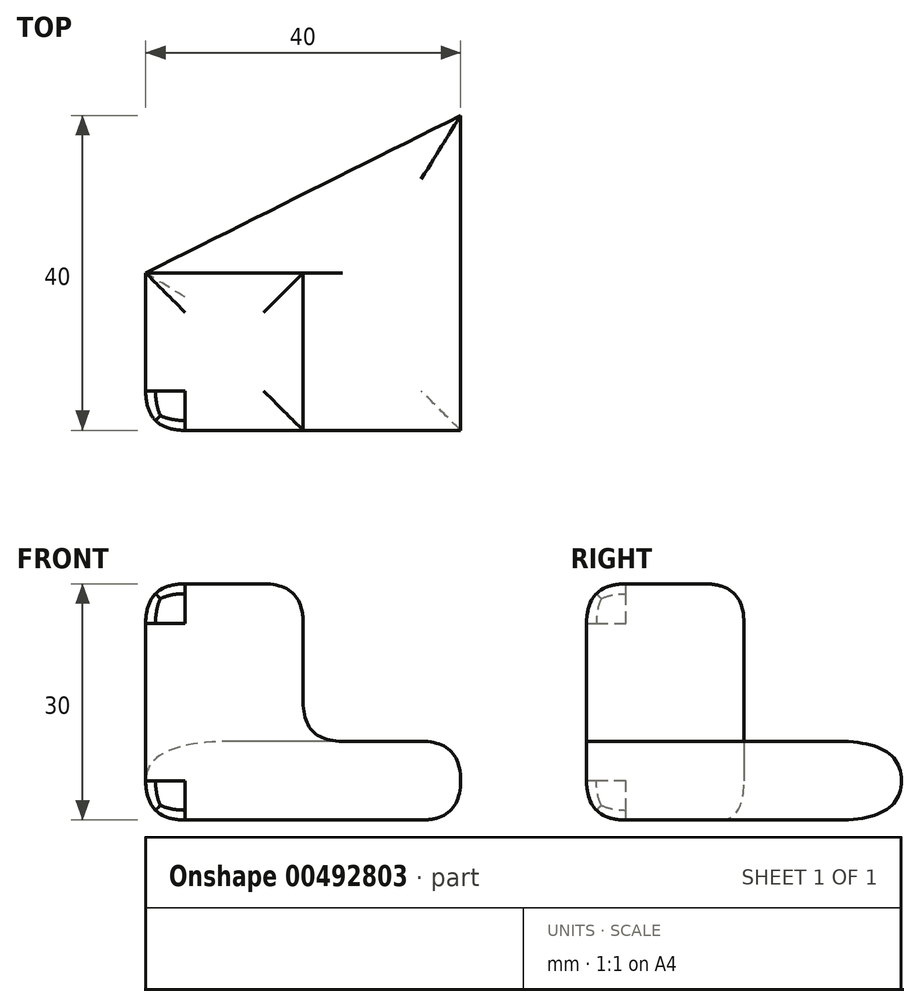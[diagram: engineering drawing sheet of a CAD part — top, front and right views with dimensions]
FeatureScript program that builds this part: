
annotation { "Feature Type Name" : "Feature", "Feature Type Description" : "" }
export const myFeature = defineFeature(function(context is Context, id is Id, definition is map)
    precondition{}
    {
        {
            var Q0;
            Q0=qCreatedBy(makeId("Top.planeOp"),FACE);
            var sketch = newSketch(context, id + "F0", { "sketchPlane" : qUnion([Q0])});
            skLineSegment(sketch, "E0", {"start": v(0, 0) * mm, "end": v(0, -20) * mm});
            skLineSegment(sketch, "E1", {"start": v(0, -20) * mm, "end": v(40, -20) * mm});
            skLineSegment(sketch, "E2", {"start": v(40, -20) * mm, "end": v(40, 20) * mm});
            skLineSegment(sketch, "E3", {"start": v(40, 20) * mm, "end": v(0, 0) * mm});
            skSolve(sketch);
        }
        {
            var Q0;
            Q0=qCreatedBy(makeId("Top.planeOp"),FACE);
            var sketch = newSketch(context, id + "F1", { "sketchPlane" : qUnion([Q0])});
            skLineSegment(sketch, "E4", {"start": v(0, 0) * mm, "end": v(20, 0) * mm});
            skLineSegment(sketch, "E5", {"start": v(20, 0) * mm, "end": v(20, -20) * mm});
            skLineSegment(sketch, "E6", {"start": v(20, -20) * mm, "end": v(0, -20) * mm});
            skLineSegment(sketch, "E7", {"start": v(0, -20) * mm, "end": v(0, 0) * mm});
            skSolve(sketch);
        }
        {
            var Q0;
            Q0=qSketchRegion(id+"F0",true);
            extrude(context, id + "F2", {"entities" : qUnion([Q0]), "depth" : 10 * mm});
        }
        {
            var Q0;
            Q0=qSketchRegion(id+"F1",true);
            extrude(context, id + "F3", {"entities" : qUnion([Q0]), "operationType" : NewBodyOperationType.ADD, "depth" : 30 * mm});
        }
        {
            var Q0;
            Q0=makeQuery(id+"F2.opExtrude","CAP_EDGE",EDGE,{"disambiguationData":[OSD([sQuery(id+"F0.wireOp",EDGE,"E2")])],"isStart":false});
            var Q1;
            Q1=makeQuery(id+"F3.boolean.opBoolean","INTERSECT",EDGE,{"derivedFrom":[makeQuery(id+"F2.opExtrude","CAP_FACE",FACE,{"disambiguationData":[OSD([sQuery(id+"F0.wireOp",EDGE,"E0"),sQuery(id+"F0.wireOp",EDGE,"E1"),sQuery(id+"F0.wireOp",EDGE,"E2"),sQuery(id+"F0.wireOp",EDGE,"E3")])],"isStart":false}),makeQuery(id+"F3.opExtrude","SWEPT_FACE",FACE,{"disambiguationData":[OSD([sQuery(id+"F1.wireOp",EDGE,"E5")])]})]});
            var Q2;
            Q2=makeQuery(id+"F3.opExtrude","CAP_EDGE",EDGE,{"disambiguationData":[OSD([sQuery(id+"F1.wireOp",EDGE,"E5")])],"isStart":false});
            var Q3;
            Q3=makeQuery(id+"F2.opExtrude","CAP_EDGE",EDGE,{"disambiguationData":[OSD([sQuery(id+"F0.wireOp",EDGE,"E1")])],"isStart":true});
            var Q4;
            Q4=makeQuery(id+"F2.opExtrude","CAP_EDGE",EDGE,{"disambiguationData":[OSD([sQuery(id+"F0.wireOp",EDGE,"E2")])],"isStart":true});
            var Q5;
            Q5=makeQuery(id+"F3.opExtrude","CAP_EDGE",EDGE,{"disambiguationData":[OSD([sQuery(id+"F1.wireOp",EDGE,"E6")])],"isStart":false});
            var Q6;
            Q6=makeQuery(id+"F3.opExtrude","CAP_EDGE",EDGE,{"disambiguationData":[OSD([sQuery(id+"F1.wireOp",EDGE,"E7")])],"isStart":false});
            var Q7;
            Q7=makeQuery(id+"F3.opExtrude","CAP_EDGE",EDGE,{"disambiguationData":[OSD([sQuery(id+"F1.wireOp",EDGE,"E4")])],"isStart":false});
            var Q8;
            Q8=makeQuery(id+"F3.boolean.opBoolean","MERGE",EDGE,{"derivedFrom":[makeQuery(id+"F2.opExtrude","SWEPT_EDGE",EDGE,{"disambiguationData":[OSD([sQuery(id+"F0.wireOp",EDGE,"E0"),sQuery(id+"F0.wireOp",EDGE,"E1")])]}),makeQuery(id+"F3.opExtrude","SWEPT_EDGE",EDGE,{"disambiguationData":[OSD([sQuery(id+"F1.wireOp",EDGE,"E6"),sQuery(id+"F1.wireOp",EDGE,"E7")])]})]});
            var Q9;
            Q9=makeQuery(id+"F2.opExtrude","CAP_EDGE",EDGE,{"disambiguationData":[OSD([sQuery(id+"F0.wireOp",EDGE,"E3")])],"isStart":false});
            var Q10;
            Q10=makeQuery(id+"F2.opExtrude","CAP_EDGE",EDGE,{"disambiguationData":[OSD([sQuery(id+"F0.wireOp",EDGE,"E3")])],"isStart":true});
            var Q11;
            Q11=makeQuery(id+"F2.opExtrude","CAP_EDGE",EDGE,{"disambiguationData":[OSD([sQuery(id+"F0.wireOp",EDGE,"E0")])],"isStart":true});
            fillet(context, id + "F4", {"entities" : qUnion([Q0, Q1, Q2, Q3, Q4, Q5, Q6, Q7, Q8, Q9, Q10, Q11]), "radius" : 5 * mm, "tangentPropagation" : true, "rho" : 0.5, "crossSection" : FilletCrossSection.CONIC, "allowEdgeOverflow" : false});
        }
    });
